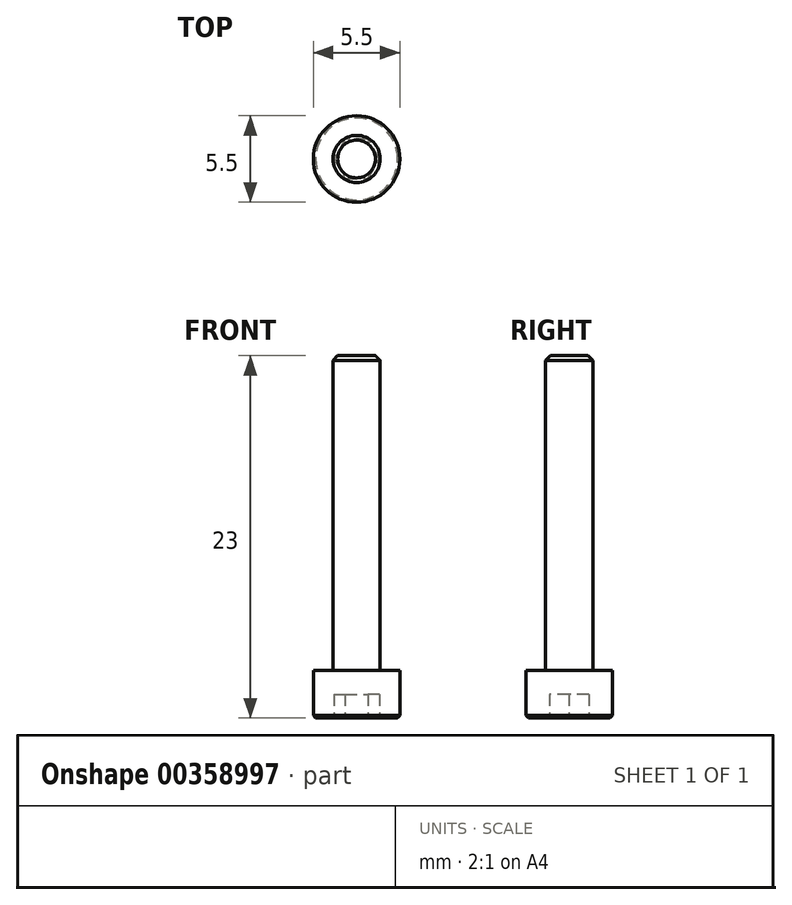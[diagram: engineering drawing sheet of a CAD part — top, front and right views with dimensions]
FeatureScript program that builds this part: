
annotation { "Feature Type Name" : "Feature", "Feature Type Description" : "" }
export const myFeature = defineFeature(function(context is Context, id is Id, definition is map)
    precondition{}
    {
        {
            assignVariable(context, id + "F0", {"name" : "d", "anyValue" : 3});
        }
        {
            assignVariable(context, id + "F1", {"name" : "a", "anyValue" : getVariable(context, 'd')});
        }
        {
            assignVariable(context, id + "F2", {"name" : "L", "anyValue" : 20});
        }
        {
            var Q0;
            Q0=qCreatedBy(makeId("Top.planeOp"),FACE);
            var sketch = newSketch(context, id + "F3", { "sketchPlane" : qUnion([Q0])});
            skCircle(sketch, "E0", {"center": v(0, 0) * mm, "radius": 2.75 * mm});
            skSolve(sketch);
        }
        {
            var Q0;
            Q0 = qSketchRegion(id + "F3", true);
            extrude(context, id + "F4", {"entities" : qUnion([Q0]), "depth" : (getVariable(context, 'a')) * mm});
        }
        {
            var Q0;
            Q0=makeQuery(id+"F4.opExtrude","CAP_FACE",FACE,{"disambiguationData":[OSD([sQuery(id+"F3.wireOp",EDGE,"E0")])],"isStart":true});
            var sketch = newSketch(context, id + "F5", { "sketchPlane" : qUnion([Q0])});
            skCircle(sketch, "E1.cCircle", {"center": v(0, 0) * mm, "radius": 1.25 * mm, "construction": true});
            skLineSegment(sketch, "E1.0", {"start": v(-0.72, 1.25) * mm, "end": v(0.72, 1.25) * mm});
            skLineSegment(sketch, "E1.1", {"start": v(0.72, 1.25) * mm, "end": v(1.44, 0) * mm});
            skLineSegment(sketch, "E1.2", {"start": v(1.44, 0) * mm, "end": v(0.72, -1.25) * mm});
            skLineSegment(sketch, "E1.3", {"start": v(0.72, -1.25) * mm, "end": v(-0.72, -1.25) * mm});
            skLineSegment(sketch, "E1.4", {"start": v(-0.72, -1.25) * mm, "end": v(-1.44, 0) * mm});
            skLineSegment(sketch, "E1.5", {"start": v(-1.44, 0) * mm, "end": v(-0.72, 1.25) * mm});
            skPoint(sketch, "E1.0.midPoint", {"position": v(0, 1.25) * mm});
            skSolve(sketch);
        }
        {
            var Q0;
            Q0 = qSketchRegion(id + "F5", true);
            extrude(context, id + "F6", {"entities" : qUnion([Q0]), "operationType" : NewBodyOperationType.REMOVE, "oppositeDirection" : true, "depth" : (getVariable(context, 'a') / 2) * mm});
        }
        {
            var Q0;
            Q0=makeQuery(id+"F4.opExtrude","CAP_FACE",FACE,{"disambiguationData":[OSD([sQuery(id+"F3.wireOp",EDGE,"E0")])],"isStart":false});
            var sketch = newSketch(context, id + "F7", { "sketchPlane" : qUnion([Q0])});
            skCircle(sketch, "E2", {"center": v(0, 0) * mm, "radius": 1.5 * mm});
            skSolve(sketch);
        }
        {
            var Q0;
            Q0 = qSketchRegion(id + "F7", true);
            extrude(context, id + "F8", {"entities" : qUnion([Q0]), "operationType" : NewBodyOperationType.ADD, "depth" : (getVariable(context, 'L')) * mm});
        }
        {
            var Q0;
            Q0=makeQuery(id+"F4.opExtrude","CAP_EDGE",EDGE,{"disambiguationData":[OSD([sQuery(id+"F3.wireOp",EDGE,"E0")])],"isStart":true});
            var Q1;
            Q1=makeQuery(id+"F6.boolean.opBoolean","COPY",EDGE,{"derivedFrom":makeQuery(id+"F6.opExtrude","CAP_EDGE",EDGE,{"disambiguationData":[OSD([sQuery(id+"F5.wireOp",EDGE,"E1.0")])],"isStart":true})});
            var Q2;
            Q2=makeQuery(id+"F6.boolean.opBoolean","COPY",EDGE,{"derivedFrom":makeQuery(id+"F6.opExtrude","CAP_EDGE",EDGE,{"disambiguationData":[OSD([sQuery(id+"F5.wireOp",EDGE,"E1.1")])],"isStart":true})});
            var Q3;
            Q3=makeQuery(id+"F6.boolean.opBoolean","COPY",EDGE,{"derivedFrom":makeQuery(id+"F6.opExtrude","CAP_EDGE",EDGE,{"disambiguationData":[OSD([sQuery(id+"F5.wireOp",EDGE,"E1.2")])],"isStart":true})});
            var Q4;
            Q4=makeQuery(id+"F6.boolean.opBoolean","COPY",EDGE,{"derivedFrom":makeQuery(id+"F6.opExtrude","CAP_EDGE",EDGE,{"disambiguationData":[OSD([sQuery(id+"F5.wireOp",EDGE,"E1.3")])],"isStart":true})});
            var Q5;
            Q5=makeQuery(id+"F6.boolean.opBoolean","COPY",EDGE,{"derivedFrom":makeQuery(id+"F6.opExtrude","CAP_EDGE",EDGE,{"disambiguationData":[OSD([sQuery(id+"F5.wireOp",EDGE,"E1.5")])],"isStart":true})});
            var Q6;
            Q6=makeQuery(id+"F6.boolean.opBoolean","COPY",EDGE,{"derivedFrom":makeQuery(id+"F6.opExtrude","CAP_EDGE",EDGE,{"disambiguationData":[OSD([sQuery(id+"F5.wireOp",EDGE,"E1.4")])],"isStart":true})});
            chamfer(context, id + "F9", {"entities" : qUnion([Q0, Q1, Q2, Q3, Q4, Q5, Q6]), "width" : (getVariable(context, 'd') / 20) * mm, "tangentPropagation" : true});
        }
        {
            var Q0;
            Q0=makeQuery(id+"F8.opExtrude","CAP_EDGE",EDGE,{"disambiguationData":[OSD([sQuery(id+"F7.wireOp",EDGE,"E2")])],"isStart":false});
            chamfer(context, id + "F10", {"entities" : qUnion([Q0]), "width" : (getVariable(context, 'd') / 10) * mm, "tangentPropagation" : true});
        }
    });
